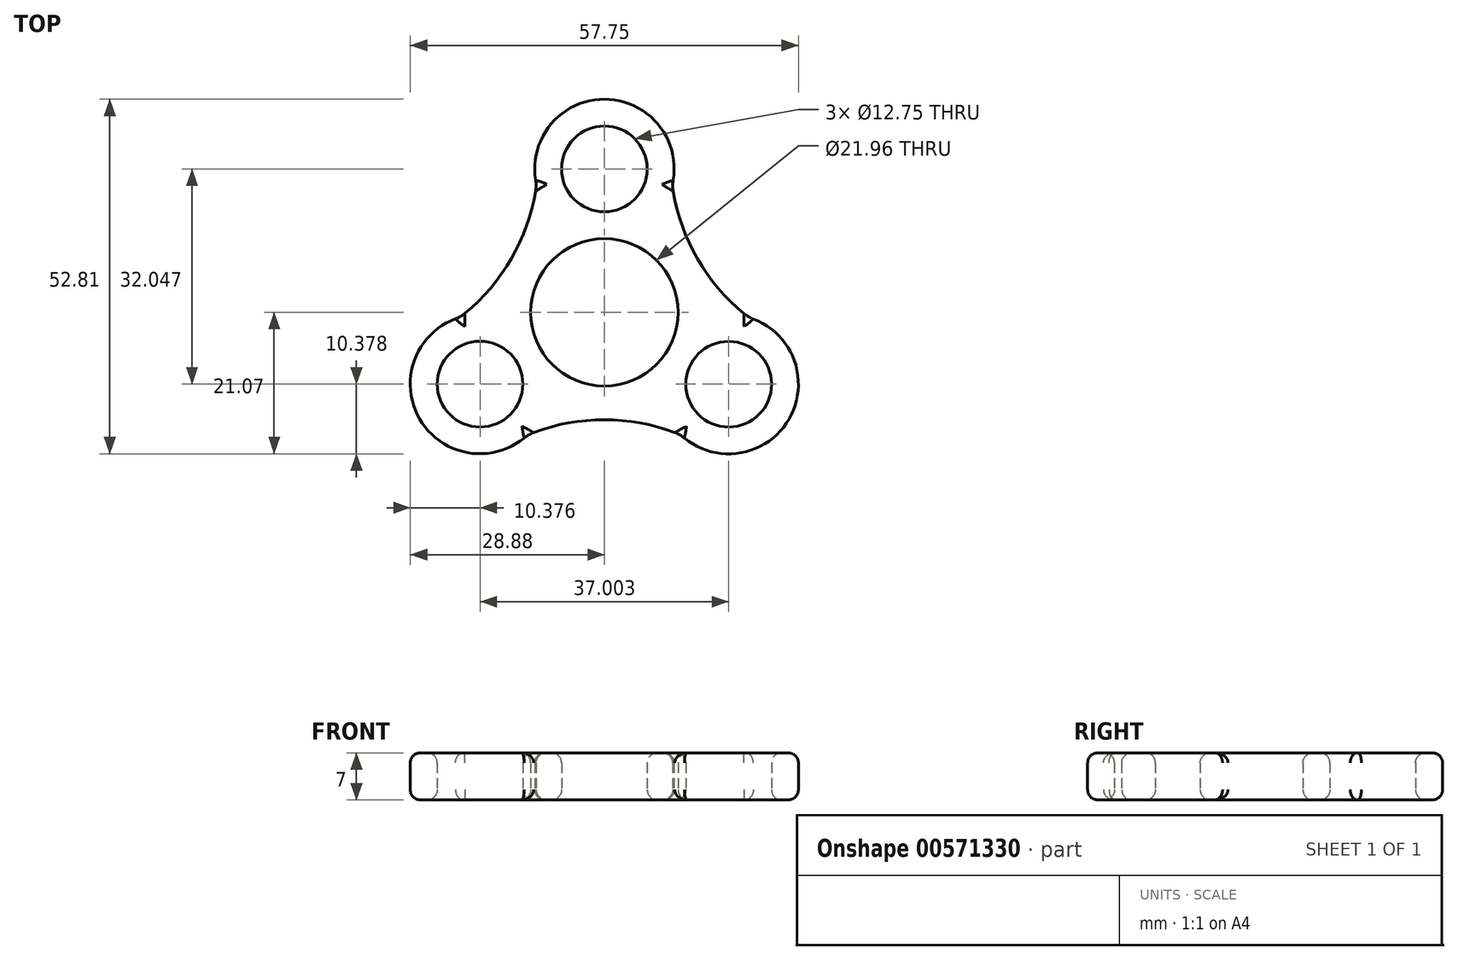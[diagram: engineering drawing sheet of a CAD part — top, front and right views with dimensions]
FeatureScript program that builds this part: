
annotation { "Feature Type Name" : "Feature", "Feature Type Description" : "" }
export const myFeature = defineFeature(function(context is Context, id is Id, definition is map)
    precondition{}
    {
        {
            var Q0;
            Q0=qCreatedBy(makeId("Top.planeOp"),FACE);
            var sketch = newSketch(context, id + "F0", { "sketchPlane" : qUnion([Q0])});
            skCircle(sketch, "E0", {"center": v(0, 0) * mm, "radius": 10.98 * mm});
            skCircle(sketch, "E1", {"center": v(0, 21.35) * mm, "radius": 6.38 * mm});
            skCircle(sketch, "E2.1.0", {"center": v(-18.5, -10.69) * mm, "radius": 6.38 * mm});
            skCircle(sketch, "E2.2.0", {"center": v(18.5, -10.7) * mm, "radius": 6.38 * mm});
            skArc(sketch, "E3", {"start": v(11.37, -18.23) * mm, "mid": v(27.48, -15.9) * mm, "end": v(21.49, -0.76) * mm});
            skArc(sketch, "E4.1.0", {"start": v(-0.03, 10.98) * mm, "mid": v(0.02, 10.98) * mm, "end": v(0.06, 10.98) * mm});
            skPoint(sketch, "E4.center", {"position": v(0.01, 0) * mm});
            skArc(sketch, "E5.1.0", {"start": v(10.1, 18.96) * mm, "mid": v(10.1, 18.93) * mm, "end": v(10.11, 18.9) * mm});
            skLineSegment(sketch, "E5.2.0", {"start": v(-21.47, -0.73) * mm, "end": v(-21.47, -0.73) * mm});
            skArc(sketch, "E6", {"start": v(10.1, 18.96) * mm, "mid": v(13.85, 7.98) * mm, "end": v(21.49, -0.76) * mm});
            skPoint(sketch, "E7.orphan", {"position": v(21.48, -0.75) * mm});
            skArc(sketch, "E8.trimOffspring", {"start": v(-9.33, -5.8) * mm, "mid": v(-9.5, -5.48) * mm, "end": v(-9.69, -5.17) * mm});
            skArc(sketch, "E9.1.0", {"start": v(-21.47, -0.73) * mm, "mid": v(-13.84, 8) * mm, "end": v(-10.09, 18.99) * mm});
            skArc(sketch, "E9.1.1", {"start": v(10.1, 18.96) * mm, "mid": v(0.02, 31.74) * mm, "end": v(-10.09, 18.99) * mm});
            skArc(sketch, "E9.2.0", {"start": v(11.37, -18.23) * mm, "mid": v(-0.01, -15.99) * mm, "end": v(-11.4, -18.23) * mm});
            skArc(sketch, "E9.2.1", {"start": v(-21.47, -0.73) * mm, "mid": v(-27.5, -15.85) * mm, "end": v(-11.4, -18.23) * mm});
            skSolve(sketch);
        }
        {
            var Q0;
            Q0=qSketchRegion(id+"F0",true);
            extrude(context, id + "F1", {"entities" : qUnion([Q0]), "depth" : 7 * mm, "offsetDistance" : 25 * mm});
        }
        {
            var Q0;
            Q0=makeQuery(id+"F1.opExtrude","CAP_FACE",FACE,{"disambiguationData":[OSD([sQuery(id+"F0.wireOp",EDGE,"E0"),sQuery(id+"F0.wireOp",EDGE,"E1"),sQuery(id+"F0.wireOp",EDGE,"E2.1.0"),sQuery(id+"F0.wireOp",EDGE,"E2.2.0"),sQuery(id+"F0.wireOp",EDGE,"E3"),sQuery(id+"F0.wireOp",EDGE,"E6"),sQuery(id+"F0.wireOp",EDGE,"E9.1.0"),sQuery(id+"F0.wireOp",EDGE,"E9.1.1"),sQuery(id+"F0.wireOp",EDGE,"E9.2.0"),sQuery(id+"F0.wireOp",EDGE,"E9.2.1")])],"isStart":false});
            var Q1;
            Q1=makeQuery(id+"F1.opExtrude","CAP_FACE",FACE,{"disambiguationData":[OSD([sQuery(id+"F0.wireOp",EDGE,"E0"),sQuery(id+"F0.wireOp",EDGE,"E1"),sQuery(id+"F0.wireOp",EDGE,"E2.1.0"),sQuery(id+"F0.wireOp",EDGE,"E2.2.0"),sQuery(id+"F0.wireOp",EDGE,"E3"),sQuery(id+"F0.wireOp",EDGE,"E6"),sQuery(id+"F0.wireOp",EDGE,"E9.1.0"),sQuery(id+"F0.wireOp",EDGE,"E9.1.1"),sQuery(id+"F0.wireOp",EDGE,"E9.2.0"),sQuery(id+"F0.wireOp",EDGE,"E9.2.1")])],"isStart":true});
            fillet(context, id + "F2", {"entities" : qUnion([Q0, Q1]), "radius" : 1.5 * mm, "tangentPropagation" : true, "allowEdgeOverflow" : false});
        }
        {
            var Q0;
            Q0=makeQuery(id+"F1.opExtrude","SWEPT_EDGE",EDGE,{"disambiguationData":[OSD([sQuery(id+"F0.wireOp",EDGE,"E9.1.0"),sQuery(id+"F0.wireOp",EDGE,"E9.1.1")])]});
            var Q1;
            Q1=makeQuery(id+"F1.opExtrude","SWEPT_EDGE",EDGE,{"disambiguationData":[OSD([sQuery(id+"F0.wireOp",EDGE,"E6"),sQuery(id+"F0.wireOp",EDGE,"E9.1.1")])]});
            var Q2;
            Q2=makeQuery(id+"F1.opExtrude","SWEPT_EDGE",EDGE,{"disambiguationData":[OSD([sQuery(id+"F0.wireOp",EDGE,"E3"),sQuery(id+"F0.wireOp",EDGE,"E6")])]});
            var Q3;
            Q3=makeQuery(id+"F1.opExtrude","SWEPT_EDGE",EDGE,{"disambiguationData":[OSD([sQuery(id+"F0.wireOp",EDGE,"E3"),sQuery(id+"F0.wireOp",EDGE,"E9.2.0")])]});
            var Q4;
            Q4=makeQuery(id+"F1.opExtrude","SWEPT_EDGE",EDGE,{"disambiguationData":[OSD([sQuery(id+"F0.wireOp",EDGE,"E9.2.0"),sQuery(id+"F0.wireOp",EDGE,"E9.2.1")])]});
            var Q5;
            Q5=makeQuery(id+"F1.opExtrude","SWEPT_EDGE",EDGE,{"disambiguationData":[OSD([sQuery(id+"F0.wireOp",EDGE,"E9.1.0"),sQuery(id+"F0.wireOp",EDGE,"E9.2.1")])]});
            fillet(context, id + "F3", {"entities" : qUnion([Q0, Q1, Q2, Q3, Q4, Q5]), "radius" : 5 * mm, "tangentPropagation" : true, "allowEdgeOverflow" : false});
        }
    });
